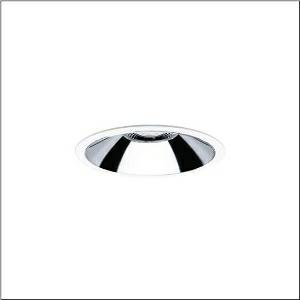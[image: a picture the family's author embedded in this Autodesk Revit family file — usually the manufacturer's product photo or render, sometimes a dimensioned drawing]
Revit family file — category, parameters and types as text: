
# Revit family: lunis_21_xl_51db15df32
name_source: partatom
category: Lighting Fixtures
units: mm (PartAtom-declared; Revit-internal decimal feet)

## family parameters
Cut with Voids When Loaded = No
Host = Face
Light Source = No
Part Type = Normal
Room Calculation Point = No
Round Connector Dimension = Use Diameter
Shared = No

## types (1)
- Lunis 21 XL (1 x LED, 2180 lm, 19.1 W, 3000K)
    Apparent Load = 19 VA
    CIE Flux Codes = 89 99 100 100 100
    Color Rendering = 80
    Color Temperature = 3000K
    Default Elevation = 1800 mm
    Description = Lunis 21,  XL, downlight, of PC, light emission: direct distribution, LED rated luminous flux: 2.180lm, light colour: 830, control gear: ECG DALI, with terminal, 5-pole, mains connection: 220..240V, AC, housing, round, of diecast aluminium, traffic white (RAL 9016), diameter: 213mm, protection rating (complete): IP20, insulation class (complete): insulation class II (safety insulation), certification: CE, impact resistance: IK02, packaging unit: 1 piece
    Height = 0 mm  [stored 0 ft]
    Lamp = 1 x LED
    Lamp Light Flux = 2180 lm
    Lamp Power = 19.1 W
    Lamp count = 1
    Length = 213 mm
    Luminous efficacy = 114 lm/W
    Manufacturer = Siteco
    ModVariant = No
    Model = 51DB15DF32
    Mounting Place = Ceiling
    Mounting Type = Recessed
    Number of Poles = 1
    OnlyDefault = Yes
    Power Factor = 1
    Product Name = Lunis 21 XL
    Product group = downlight | ceiling recessed
    ProductGroupID = 402
    Protection Class = Protection class II
    Protection Degree = IP 20
    RLX_Detail_Level = 1
    RlxData = <blob elided: 27065 chars, md5=4b462bb2>
    Socket = socket
    Standby Power = 0 W
    System Light Flux = 2180 lm
    System Power = 19 W
    Type Comments = Product without accessories
    Type Image = l_1006990.jpg
    URL = http://relux.com
    VarID = ---
    Voltage = 0 V
    Weight = 0.00 kg
    Width = 0 mm  [stored 0 ft]

note: [stored X ft] marks values corroborated as IEEE doubles in the binary element streams (Revit-internal decimal feet)

## geometry (parser evidence)
native form markers: Blend x4, Sweep x11
no freeform markers — native parametric forms only
